FCSTD DOCUMENT  (FreeCAD 0.16R6712 (Git))
Label: connector panels
License: All rights reserved
LicenseURL: http://en.wikipedia.org/wiki/All_rights_reserved
objects: Sketcher::SketchObject×2
note: 2 computed .brp shape members not serialized (recipe doc carries the construction recipe); baked Part::Feature solids carry a one-line shape summary decoded from their .brp

FEATURE [Sketcher::SketchObject] Sketch  label="motors"
  sketch-geometry (109):
    g0: LineSegment StartX=-80 StartY=50 StartZ=0 EndX=80 EndY=50 EndZ=0
    g1: LineSegment StartX=85 StartY=45 StartZ=0 EndX=85 EndY=-45 EndZ=0
    g2: LineSegment StartX=80 StartY=-50 StartZ=0 EndX=-80 EndY=-50 EndZ=0
    g3: LineSegment StartX=-85 StartY=-45 StartZ=0 EndX=-85 EndY=45 EndZ=0
    g4: LineSegment [constr] StartX=-80 StartY=40 StartZ=0 EndX=80 EndY=40 EndZ=0
    g5: LineSegment [constr] StartX=80 StartY=40 StartZ=0 EndX=80 EndY=-40 EndZ=0
    g6: LineSegment [constr] StartX=80 StartY=-40 StartZ=0 EndX=-80 EndY=-40 EndZ=0
    g7: LineSegment [constr] StartX=-80 StartY=-40 StartZ=0 EndX=-80 EndY=40 EndZ=0
    g8: LineSegment [constr] StartX=-80 StartY=40 StartZ=0 EndX=-80 EndY=45 EndZ=0
    g9: LineSegment [constr] StartX=80 StartY=40 StartZ=0 EndX=80 EndY=45 EndZ=0
    g10: LineSegment [constr] StartX=80 StartY=-40 StartZ=0 EndX=80 EndY=-45 EndZ=0
    g11: LineSegment [constr] StartX=-80 StartY=-40 StartZ=0 EndX=-80 EndY=-45 EndZ=0
    g12: Circle CenterX=-80 CenterY=45 CenterZ=0 NormalX=0 NormalY=0 NormalZ=1 Radius=1.5
    g13: Circle CenterX=80 CenterY=45 CenterZ=0 NormalX=0 NormalY=0 NormalZ=1 Radius=1.5
    g14: Circle CenterX=80 CenterY=-45 CenterZ=0 NormalX=0 NormalY=0 NormalZ=1 Radius=1.5
    g15: Circle CenterX=-80 CenterY=-45 CenterZ=0 NormalX=0 NormalY=0 NormalZ=1 Radius=1.5
    g16: LineSegment StartX=-63.2009 StartY=-7.15277 StartZ=0 EndX=-59.4009 EndY=-7.82282 EndZ=0
    g17: LineSegment StartX=-57.1698 StartY=-10.4818 StartZ=0 EndX=-57.1698 EndY=-21.6417 EndZ=0
    g18: LineSegment StartX=-59.4009 StartY=-24.3007 StartZ=0 EndX=-63.2009 EndY=-24.9707 EndZ=0
    g19: LineSegment StartX=-66.3698 StartY=-22.3118 StartZ=0 EndX=-66.3698 EndY=-9.81175 EndZ=0
    g20: ArcOfCircle CenterX=-59.8698 CenterY=-10.4818 CenterZ=0 NormalX=0 NormalY=0 NormalZ=1 Radius=2.7 StartAngle=0 EndAngle=1.39626
    g21: ArcOfCircle CenterX=-63.6698 CenterY=-9.81175 CenterZ=0 NormalX=0 NormalY=0 NormalZ=1 Radius=2.7 StartAngle=1.39626 EndAngle=3.14159
    g22: ArcOfCircle CenterX=-59.8698 CenterY=-21.6417 CenterZ=0 NormalX=0 NormalY=0 NormalZ=1 Radius=2.7 StartAngle=4.88692 EndAngle=6.28319
    g23: ArcOfCircle CenterX=-63.6698 CenterY=-22.3118 CenterZ=0 NormalX=0 NormalY=0 NormalZ=1 Radius=2.7 StartAngle=3.14159 EndAngle=4.88692
    g24: Circle CenterX=-61.7698 CenterY=-3.6506 CenterZ=0 NormalX=0 NormalY=0 NormalZ=1 Radius=1.5
    g25: Circle CenterX=-61.7698 CenterY=-28.6506 CenterZ=0 NormalX=0 NormalY=0 NormalZ=1 Radius=1.5
    g26: LineSegment [constr] StartX=-61.7698 StartY=-3.6506 StartZ=0 EndX=-61.7698 EndY=-28.6506 EndZ=0
    g27: Circle CenterX=-61.7698 CenterY=21.3494 CenterZ=0 NormalX=0 NormalY=0 NormalZ=1 Radius=8
    g28: LineSegment [constr] StartX=-61.7698 StartY=21.3494 StartZ=0 EndX=-61.7698 EndY=-3.6506 EndZ=0
    g29: LineSegment [constr] StartX=80 StartY=-45 StartZ=0 EndX=-80 EndY=-45 EndZ=0
    g30: LineSegment [constr] StartX=-80 StartY=45 StartZ=0 EndX=80 EndY=45 EndZ=0
    g31: Circle CenterX=0 CenterY=45 CenterZ=0 NormalX=0 NormalY=0 NormalZ=1 Radius=1.5
    g32: Circle CenterX=0 CenterY=-45 CenterZ=0 NormalX=0 NormalY=0 NormalZ=1 Radius=1.5
    g33: Circle CenterX=-30.8849 CenterY=21.3494 CenterZ=0 NormalX=0 NormalY=0 NormalZ=1 Radius=8
    g34: LineSegment [constr] StartX=-30.8849 StartY=21.3494 StartZ=0 EndX=-30.8849 EndY=-3.6506 EndZ=0
    g35: Circle CenterX=0 CenterY=21.3494 CenterZ=0 NormalX=0 NormalY=0 NormalZ=1 Radius=8
    g36: LineSegment [constr] StartX=0 StartY=21.3494 StartZ=0 EndX=0 EndY=-3.6506 EndZ=0
    g37: Circle CenterX=30.8849 CenterY=21.3494 CenterZ=0 NormalX=0 NormalY=0 NormalZ=1 Radius=8
    g38: LineSegment [constr] StartX=30.8849 StartY=21.3494 StartZ=0 EndX=30.8849 EndY=-3.6506 EndZ=0
    g39: Circle CenterX=61.7698 CenterY=21.3494 CenterZ=0 NormalX=0 NormalY=0 NormalZ=1 Radius=10
    g40: LineSegment [constr] StartX=-80 StartY=21.3494 StartZ=0 EndX=-61.7698 EndY=21.3494 EndZ=0
    g41: LineSegment [constr] StartX=-61.7698 StartY=21.3494 StartZ=0 EndX=-30.8849 EndY=21.3494 EndZ=0
    g42: LineSegment [constr] StartX=-30.8849 StartY=21.3494 StartZ=0 EndX=0 EndY=21.3494 EndZ=0
    g43: LineSegment [constr] StartX=0 StartY=21.3494 StartZ=0 EndX=30.8849 EndY=21.3494 EndZ=0
    g44: LineSegment [constr] StartX=30.8849 StartY=21.3494 StartZ=0 EndX=61.7698 EndY=21.3494 EndZ=0
    g45: LineSegment [constr] StartX=61.7698 StartY=21.3494 StartZ=0 EndX=80 EndY=21.3494 EndZ=0
    g46: LineSegment [constr] StartX=61.7698 StartY=21.3494 StartZ=0 EndX=61.7698 EndY=-15.6506 EndZ=0
    g47: Circle CenterX=61.7698 CenterY=-15.6506 CenterZ=0 NormalX=0 NormalY=0 NormalZ=1 Radius=1.5
    g48: LineSegment [constr] StartX=-63.6698 StartY=-7.11175 StartZ=0 EndX=-61.7698 EndY=-7.11175 EndZ=0
    g49: LineSegment [constr] StartX=-63.6698 StartY=-25.0118 StartZ=0 EndX=-61.7698 EndY=-25.0118 EndZ=0
    g50: LineSegment [constr] StartX=-66.3698 StartY=-21.6417 StartZ=0 EndX=-61.7698 EndY=-21.6417 EndZ=0
    g51: LineSegment [constr] StartX=-61.7698 StartY=-21.6417 StartZ=0 EndX=-57.1698 EndY=-21.6417 EndZ=0
    g52: LineSegment [constr] StartX=-63.2009 StartY=-24.9707 StartZ=0 EndX=-61.7698 EndY=-28.6506 EndZ=0
    g53: LineSegment [constr] StartX=-63.6698 StartY=-7.11175 StartZ=0 EndX=-61.7698 EndY=-3.6506 EndZ=0
    g54: LineSegment StartX=-32.316 StartY=-7.15277 StartZ=0 EndX=-28.516 EndY=-7.82282 EndZ=0
    g55: LineSegment StartX=-26.2849 StartY=-10.4818 StartZ=0 EndX=-26.2849 EndY=-21.6417 EndZ=0
    g56: LineSegment StartX=-28.516 StartY=-24.3007 StartZ=0 EndX=-32.316 EndY=-24.9707 EndZ=0
    g57: LineSegment StartX=-35.4849 StartY=-22.3118 StartZ=0 EndX=-35.4849 EndY=-9.81175 EndZ=0
    g58: ArcOfCircle CenterX=-28.9849 CenterY=-10.4818 CenterZ=0 NormalX=0 NormalY=0 NormalZ=1 Radius=2.7 StartAngle=0 EndAngle=1.39626
    g59: ArcOfCircle CenterX=-32.7849 CenterY=-9.81175 CenterZ=0 NormalX=0 NormalY=0 NormalZ=1 Radius=2.7 StartAngle=1.39626 EndAngle=3.14159
    g60: ArcOfCircle CenterX=-28.9849 CenterY=-21.6417 CenterZ=0 NormalX=0 NormalY=0 NormalZ=1 Radius=2.7 StartAngle=4.88692 EndAngle=6.28319
    g61: ArcOfCircle CenterX=-32.7849 CenterY=-22.3118 CenterZ=0 NormalX=0 NormalY=0 NormalZ=1 Radius=2.7 StartAngle=3.14159 EndAngle=4.88692
    g62: Circle CenterX=-30.8849 CenterY=-3.6506 CenterZ=0 NormalX=0 NormalY=0 NormalZ=1 Radius=1.5
    g63: Circle CenterX=-30.8849 CenterY=-28.6506 CenterZ=0 NormalX=0 NormalY=0 NormalZ=1 Radius=1.5
    g64: LineSegment [constr] StartX=-30.8849 StartY=-3.6506 StartZ=0 EndX=-30.8849 EndY=-28.6506 EndZ=0
    g65: LineSegment [constr] StartX=-32.7849 StartY=-7.11175 StartZ=0 EndX=-30.8849 EndY=-7.11175 EndZ=0
    g66: LineSegment [constr] StartX=-32.7849 StartY=-25.0118 StartZ=0 EndX=-30.8849 EndY=-25.0118 EndZ=0
    g67: LineSegment [constr] StartX=-35.4849 StartY=-21.6417 StartZ=0 EndX=-30.8849 EndY=-21.6417 EndZ=0
    g68: LineSegment [constr] StartX=-30.8849 StartY=-21.6417 StartZ=0 EndX=-26.2849 EndY=-21.6417 EndZ=0
    g69: LineSegment [constr] StartX=-32.316 StartY=-24.9707 StartZ=0 EndX=-30.8849 EndY=-28.6506 EndZ=0
    g70: LineSegment [constr] StartX=-32.7849 StartY=-7.11175 StartZ=0 EndX=-30.8849 EndY=-3.6506 EndZ=0
    g71: LineSegment StartX=-1.43115 StartY=-7.15277 StartZ=0 EndX=2.36885 EndY=-7.82282 EndZ=0
    g72: LineSegment StartX=4.6 StartY=-10.4818 StartZ=0 EndX=4.6 EndY=-21.6417 EndZ=0
    g73: LineSegment StartX=2.36885 StartY=-24.3007 StartZ=0 EndX=-1.43115 EndY=-24.9707 EndZ=0
    g74: LineSegment StartX=-4.6 StartY=-22.3118 StartZ=0 EndX=-4.6 EndY=-9.81175 EndZ=0
    g75: ArcOfCircle CenterX=1.9 CenterY=-10.4818 CenterZ=0 NormalX=0 NormalY=0 NormalZ=1 Radius=2.7 StartAngle=0 EndAngle=1.39626
    g76: ArcOfCircle CenterX=-1.9 CenterY=-9.81175 CenterZ=0 NormalX=0 NormalY=0 NormalZ=1 Radius=2.7 StartAngle=1.39626 EndAngle=3.14159
    g77: ArcOfCircle CenterX=1.9 CenterY=-21.6417 CenterZ=0 NormalX=0 NormalY=0 NormalZ=1 Radius=2.7 StartAngle=4.88692 EndAngle=6.28319
    g78: ArcOfCircle CenterX=-1.9 CenterY=-22.3118 CenterZ=0 NormalX=0 NormalY=0 NormalZ=1 Radius=2.7 StartAngle=3.14159 EndAngle=4.88692
    g79: Circle CenterX=0 CenterY=-3.6506 CenterZ=0 NormalX=0 NormalY=0 NormalZ=1 Radius=1.5
    g80: Circle CenterX=0 CenterY=-28.6506 CenterZ=0 NormalX=0 NormalY=0 NormalZ=1 Radius=1.5
    g81: LineSegment [constr] StartX=0 StartY=-3.6506 StartZ=0 EndX=0 EndY=-28.6506 EndZ=0
    g82: LineSegment [constr] StartX=-1.9 StartY=-7.11175 StartZ=0 EndX=0 EndY=-7.11175 EndZ=0
    g83: LineSegment [constr] StartX=-1.9 StartY=-25.0118 StartZ=0 EndX=0 EndY=-25.0118 EndZ=0
    g84: LineSegment [constr] StartX=-4.6 StartY=-21.6417 StartZ=0 EndX=0 EndY=-21.6417 EndZ=0
    g85: LineSegment [constr] StartX=0 StartY=-21.6417 StartZ=0 EndX=4.6 EndY=-21.6417 EndZ=0
    g86: LineSegment [constr] StartX=-1.43115 StartY=-24.9707 StartZ=0 EndX=0 EndY=-28.6506 EndZ=0
    g87: LineSegment [constr] StartX=-1.9 StartY=-7.11175 StartZ=0 EndX=0 EndY=-3.6506 EndZ=0
    g88: LineSegment StartX=29.4538 StartY=-7.15277 StartZ=0 EndX=33.2538 EndY=-7.82282 EndZ=0
    g89: LineSegment StartX=35.4849 StartY=-10.4818 StartZ=0 EndX=35.4849 EndY=-21.6417 EndZ=0
    g90: LineSegment StartX=33.2538 StartY=-24.3007 StartZ=0 EndX=29.4538 EndY=-24.9707 EndZ=0
    g91: LineSegment StartX=26.2849 StartY=-22.3118 StartZ=0 EndX=26.2849 EndY=-9.81175 EndZ=0
    g92: ArcOfCircle CenterX=32.7849 CenterY=-10.4818 CenterZ=0 NormalX=0 NormalY=0 NormalZ=1 Radius=2.7 StartAngle=0 EndAngle=1.39626
    g93: ArcOfCircle CenterX=28.9849 CenterY=-9.81175 CenterZ=0 NormalX=0 NormalY=0 NormalZ=1 Radius=2.7 StartAngle=1.39626 EndAngle=3.14159
    g94: ArcOfCircle CenterX=32.7849 CenterY=-21.6417 CenterZ=0 NormalX=0 NormalY=0 NormalZ=1 Radius=2.7 StartAngle=4.88692 EndAngle=6.28319
    g95: ArcOfCircle CenterX=28.9849 CenterY=-22.3118 CenterZ=0 NormalX=0 NormalY=0 NormalZ=1 Radius=2.7 StartAngle=3.14159 EndAngle=4.88692
    g96: Circle CenterX=30.8849 CenterY=-3.6506 CenterZ=0 NormalX=0 NormalY=0 NormalZ=1 Radius=1.5
    g97: Circle CenterX=30.8849 CenterY=-28.6506 CenterZ=0 NormalX=0 NormalY=0 NormalZ=1 Radius=1.5
    g98: LineSegment [constr] StartX=30.8849 StartY=-3.6506 StartZ=0 EndX=30.8849 EndY=-28.6506 EndZ=0
    g99: LineSegment [constr] StartX=28.9849 StartY=-7.11175 StartZ=0 EndX=30.8849 EndY=-7.11175 EndZ=0
    g100: LineSegment [constr] StartX=28.9849 StartY=-25.0118 StartZ=0 EndX=30.8849 EndY=-25.0118 EndZ=0
    g101: LineSegment [constr] StartX=26.2849 StartY=-21.6417 StartZ=0 EndX=30.8849 EndY=-21.6417 EndZ=0
    g102: LineSegment [constr] StartX=30.8849 StartY=-21.6417 StartZ=0 EndX=35.4849 EndY=-21.6417 EndZ=0
    g103: LineSegment [constr] StartX=29.4538 StartY=-24.9707 StartZ=0 EndX=30.8849 EndY=-28.6506 EndZ=0
    g104: LineSegment [constr] StartX=28.9849 StartY=-7.11175 StartZ=0 EndX=30.8849 EndY=-3.6506 EndZ=0
    g105: ArcOfCircle CenterX=-80 CenterY=45 CenterZ=0 NormalX=0 NormalY=0 NormalZ=1 Radius=5 StartAngle=1.5708 EndAngle=3.14159
    g106: ArcOfCircle CenterX=80 CenterY=45 CenterZ=0 NormalX=0 NormalY=0 NormalZ=1 Radius=5 StartAngle=0 EndAngle=1.5708
    g107: ArcOfCircle CenterX=80 CenterY=-45 CenterZ=0 NormalX=0 NormalY=0 NormalZ=1 Radius=5 StartAngle=4.71239 EndAngle=6.28319
    g108: ArcOfCircle CenterX=-80 CenterY=-45 CenterZ=0 NormalX=0 NormalY=0 NormalZ=1 Radius=5 StartAngle=3.14159 EndAngle=4.71239
  constraints (292):
    c: Horizontal(g0)
    c: Horizontal(g2)
    c: Vertical(g1)
    c: Vertical(g3)
    c: Coincident(g4,g5)
    c: Coincident(g5,g6)
    c: Coincident(g6,g7)
    c: Coincident(g7,g4)
    c: Horizontal(g4)
    c: Horizontal(g6)
    c: Vertical(g7)
    c: Symmetric(g4,g5,g-1)
    c: Symmetric(g4,g4,g-2)
    c: DistanceY(g5,g5) = 80
    c: DistanceX(g4,g4) = 160
    c: Coincident(g8,g4)
    c: Vertical(g8)
    c: Coincident(g9,g4)
    c: Vertical(g9)
    c: Coincident(g10,g5)
    c: Vertical(g10)
    c: Coincident(g11,g6)
    c: Vertical(g11)
    c: Coincident(g12,g8)
    c: Coincident(g13,g9)
    c: Coincident(g14,g10)
    c: Coincident(g15,g11)
    c: Radius(g12) = 1.5
    c: Vertical(g17)
    c: Vertical(g19)
    c: Equal(g16,g18)
    c: Tangent(g17,g20) = 1.5708
    c: Tangent(g16,g20) = 1.5708
    c: Tangent(g16,g21) = 1.5708
    c: Tangent(g19,g21) = 1.5708
    c: Tangent(g17,g22) = 1.5708
    c: Tangent(g18,g22) = 1.5708
    c: Tangent(g18,g23) = 1.5708
    c: Tangent(g19,g23) = 1.5708
    c: Equal(g21,g23)
    c: Equal(g22,g20)
    c: Coincident(g26,g24)
    c: Coincident(g26,g25)
    c: Vertical(g26)
    c: DistanceY(g26,g26) = 25
    c: Radius(g20) = 2.7
    c: Equal(g21,g20)
    c: Coincident(g28,g27)
    c: Coincident(g28,g24)
    c: Vertical(g28)
    c: DistanceY(g28,g28) = 25
    c: Radius(g27) = 8
    c: Symmetric(g8,g11,g-1)
    c: Symmetric(g9,g10,g-1)
    c: Coincident(g29,g10)
    c: Coincident(g29,g11)
    c: Horizontal(g29)
    c: Coincident(g30,g8)
    c: Coincident(g30,g9)
    c: PointOnObject(g31,g30)
    c: PointOnObject(g31,g-2)
    c: PointOnObject(g32,g29)
    c: PointOnObject(g32,g-2)
    c: Equal(g12,g31)
    c: Equal(g12,g13)
    c: Equal(g12,g14)
    c: Equal(g12,g32)
    c: Equal(g12,g15)
    c: Radius(g24) = 1.5
    c: Equal(g24,g25)
    c: Coincident(g34,g33)
    c: Vertical(g34)
    c: Equal(g28,g34) = 25
    c: Equal(g27,g33) = 8
    c: Coincident(g36,g35)
    c: Vertical(g36)
    c: Equal(g28,g36) = 25
    c: Equal(g27,g35) = 8
    c: Coincident(g38,g37)
    c: Vertical(g38)
    c: Equal(g28,g38) = 25
    c: Equal(g27,g37) = 8
    c: Radius(g39) = 10
    c: PointOnObject(g40,g7)
    c: Coincident(g40,g27)
    c: Horizontal(g40)
    c: Coincident(g41,g27)
    c: Coincident(g41,g33)
    c: Horizontal(g41)
    c: Coincident(g42,g33)
    c: Coincident(g42,g35)
    c: Horizontal(g42)
    c: Coincident(g43,g35)
    c: Coincident(g43,g37)
    c: Horizontal(g43)
    c: Coincident(g44,g37)
    c: Coincident(g44,g39)
    c: Horizontal(g44)
    c: Coincident(g45,g39)
    c: PointOnObject(g45,g5)
    c: Horizontal(g45)
    c: Equal(g41,g42)
    c: Equal(g42,g43)
    c: Equal(g43,g44)
    c: Equal(g45,g40)
    c: Coincident(g46,g39)
    c: Vertical(g46)
    c: Coincident(g47,g46)
    c: DistanceY(g46,g46) = 37
    c: DistanceX(g42,g42) = 30.8849
    c: DistanceX(g40,g40) = 18.2302
    c: DistanceY(g45,g4) = 18.6506
    c: Radius(g47) = 1.5
    c: PointOnObject(g48,g21)
    c: PointOnObject(g48,g26)
    c: Horizontal(g48)
    c: Tangent(g48,g21)
    c: PointOnObject(g49,g23)
    c: PointOnObject(g49,g26)
    c: Horizontal(g49)
    c: Tangent(g49,g23)
    c: DistanceY(g49,g48) = 17.9
    c: DistanceX(g19,g17) = 9.2
    c: PointOnObject(g50,g19)
    c: PointOnObject(g50,g26)
    c: Horizontal(g50)
    c: Coincident(g51,g50)
    c: PointOnObject(g51,g17)
    c: Horizontal(g51)
    c: Equal(g51,g50)
    c: Coincident(g52,g18)
    c: Coincident(g52,g25)
    c: Coincident(g53,g48)
    c: Coincident(g53,g24)
    c: Equal(g53,g52)
    c: Coincident(g51,g17)
    c: Equal(g49,g48)
    c: Angle(g16,g48) = 0.174533
    c: Vertical(g55)
    c: Vertical(g57)
    c: Equal(g54,g56)
    c: Tangent(g55,g58) = 1.5708
    c: Tangent(g54,g58) = 1.5708
    c: Tangent(g54,g59) = 1.5708
    c: Tangent(g57,g59) = 1.5708
    c: Tangent(g55,g60) = 1.5708
    c: Tangent(g56,g60) = 1.5708
    c: Tangent(g56,g61) = 1.5708
    c: Tangent(g57,g61) = 1.5708
    c: Equal(g59,g61)
    c: Equal(g60,g58)
    c: Coincident(g64,g62)
    c: Coincident(g64,g63)
    c: Vertical(g64)
    c: Equal(g26,g64) = 25
    c: Equal(g20,g58) = 2.7
    c: Equal(g59,g58)
    c: Equal(g24,g62) = 1.5
    c: Equal(g62,g63)
    c: PointOnObject(g65,g64)
    c: Horizontal(g65)
    c: Tangent(g65,g59)
    c: PointOnObject(g66,g61)
    c: PointOnObject(g66,g64)
    c: Horizontal(g66)
    c: Tangent(g66,g61)
    c: DistanceY(g66,g65) = 17.9
    c: DistanceX(g57,g55) = 9.2
    c: PointOnObject(g67,g57)
    c: PointOnObject(g67,g64)
    c: Horizontal(g67)
    c: Coincident(g68,g67)
    c: PointOnObject(g68,g55)
    c: Horizontal(g68)
    c: Equal(g68,g67)
    c: Coincident(g69,g56)
    c: Coincident(g69,g63)
    c: Coincident(g70,g65)
    c: Coincident(g70,g62)
    c: Equal(g70,g69)
    c: Coincident(g68,g55)
    c: Equal(g66,g65)
    c: Angle(g54,g65) = 0.174533
    c: Coincident(g62,g34)
    c: Vertical(g72)
    c: Vertical(g74)
    c: Equal(g71,g73)
    c: Tangent(g72,g75) = 1.5708
    c: Tangent(g71,g75) = 1.5708
    c: Tangent(g71,g76) = 1.5708
    c: Tangent(g74,g76) = 1.5708
    c: Tangent(g72,g77) = 1.5708
    c: Tangent(g73,g77) = 1.5708
    c: Tangent(g73,g78) = 1.5708
    c: Tangent(g74,g78) = 1.5708
    c: Equal(g76,g78)
    c: Equal(g77,g75)
    c: Coincident(g81,g79)
    c: Coincident(g81,g80)
    c: Vertical(g81)
    c: Equal(g26,g81) = 25
    c: Equal(g20,g75) = 2.7
    c: Equal(g76,g75)
    c: Equal(g24,g79) = 1.5
    c: Equal(g79,g80)
    c: PointOnObject(g82,g81)
    c: Horizontal(g82)
    c: Tangent(g82,g76)
    c: PointOnObject(g83,g78)
    c: PointOnObject(g83,g81)
    c: Horizontal(g83)
    c: Tangent(g83,g78)
    c: DistanceY(g83,g82) = 17.9
    c: DistanceX(g74,g72) = 9.2
    c: PointOnObject(g84,g74)
    c: PointOnObject(g84,g81)
    c: Horizontal(g84)
    c: Coincident(g85,g84)
    c: PointOnObject(g85,g72)
    c: Horizontal(g85)
    c: Equal(g85,g84)
    c: Coincident(g86,g73)
    c: Coincident(g86,g80)
    c: Coincident(g87,g82)
    c: Coincident(g87,g79)
    c: Equal(g87,g86)
    c: Coincident(g85,g72)
    c: Equal(g83,g82)
    c: Angle(g71,g82) = 0.174533
    c: Coincident(g79,g36)
    c: Vertical(g89)
    c: Vertical(g91)
    c: Equal(g88,g90)
    c: Tangent(g89,g92) = 1.5708
    c: Tangent(g88,g92) = 1.5708
    c: Tangent(g88,g93) = 1.5708
    c: Tangent(g91,g93) = 1.5708
    c: Tangent(g89,g94) = 1.5708
    c: Tangent(g90,g94) = 1.5708
    c: Tangent(g90,g95) = 1.5708
    c: Tangent(g91,g95) = 1.5708
    c: Equal(g93,g95)
    c: Equal(g94,g92)
    c: Coincident(g98,g96)
    c: Coincident(g98,g97)
    c: Vertical(g98)
    c: Equal(g26,g98) = 25
    c: Equal(g20,g92) = 2.7
    c: Equal(g93,g92)
    c: Equal(g24,g96) = 1.5
    c: Equal(g96,g97)
    c: PointOnObject(g99,g98)
    c: Horizontal(g99)
    c: Tangent(g99,g93)
    c: PointOnObject(g100,g95)
    c: PointOnObject(g100,g98)
    c: Horizontal(g100)
    c: Tangent(g100,g95)
    c: DistanceY(g100,g99) = 17.9
    c: DistanceX(g91,g89) = 9.2
    c: PointOnObject(g101,g91)
    c: PointOnObject(g101,g98)
    c: Horizontal(g101)
    c: Coincident(g102,g101)
    c: PointOnObject(g102,g89)
    c: Horizontal(g102)
    c: Equal(g102,g101)
    c: Coincident(g103,g90)
    c: Coincident(g103,g97)
    c: Coincident(g104,g99)
    c: Coincident(g104,g96)
    c: Equal(g104,g103)
    c: Coincident(g102,g89)
    c: Equal(g100,g99)
    c: Angle(g88,g99) = 0.174533
    c: Coincident(g96,g38)
    c: Tangent(g3,g105) = 1.5708
    c: Tangent(g0,g105) = 1.5708
    c: Tangent(g0,g106) = 1.5708
    c: Tangent(g1,g106) = 1.5708
    c: Tangent(g1,g107) = 1.5708
    c: Tangent(g2,g107) = 1.5708
    c: Tangent(g2,g108) = 1.5708
    c: Tangent(g3,g108) = 1.5708
    c: DistanceX(g3,g1) = 170
    c: DistanceY(g2,g0) = 100
    c: Radius(g105) = 5
    c: Equal(g105,g106)
    c: Equal(g105,g107)
    c: Equal(g105,g108)
    c: Coincident(g107,g10)
    c: Coincident(g105,g8)
FEATURE [Sketcher::SketchObject] Sketch001  label="controls"
  sketch-geometry (51):
    g0: LineSegment StartX=-85 StartY=40 StartZ=0 EndX=85 EndY=40 EndZ=0
    g1: LineSegment StartX=90 StartY=35 StartZ=0 EndX=90 EndY=-35 EndZ=0
    g2: LineSegment StartX=85 StartY=-40 StartZ=0 EndX=-85 EndY=-40 EndZ=0
    g3: LineSegment StartX=-90 StartY=-35 StartZ=0 EndX=-90 EndY=35 EndZ=0
    g4: LineSegment [constr] StartX=-80 StartY=30 StartZ=0 EndX=80 EndY=30 EndZ=0
    g5: LineSegment [constr] StartX=80 StartY=30 StartZ=0 EndX=80 EndY=-30 EndZ=0
    g6: LineSegment [constr] StartX=80 StartY=-30 StartZ=0 EndX=-80 EndY=-30 EndZ=0
    g7: LineSegment [constr] StartX=-80 StartY=-30 StartZ=0 EndX=-80 EndY=30 EndZ=0
    g8: LineSegment [constr] StartX=-80 StartY=30 StartZ=0 EndX=-85 EndY=35 EndZ=0
    g9: LineSegment [constr] StartX=80 StartY=30 StartZ=0 EndX=85 EndY=35 EndZ=0
    g10: LineSegment [constr] StartX=80 StartY=-30 StartZ=0 EndX=85 EndY=-35 EndZ=0
    g11: LineSegment [constr] StartX=-80 StartY=-30 StartZ=0 EndX=-85 EndY=-35 EndZ=0
    g12: Circle CenterX=-85 CenterY=35 CenterZ=0 NormalX=0 NormalY=0 NormalZ=1 Radius=1.5
    g13: Circle CenterX=85 CenterY=35 CenterZ=0 NormalX=0 NormalY=0 NormalZ=1 Radius=1.5
    g14: Circle CenterX=85 CenterY=-35 CenterZ=0 NormalX=0 NormalY=0 NormalZ=1 Radius=1.5
    g15: Circle CenterX=-85 CenterY=-35 CenterZ=0 NormalX=0 NormalY=0 NormalZ=1 Radius=1.5
    g16: LineSegment StartX=-29.8863 StartY=12.1283 StartZ=0 EndX=-26.0863 EndY=11.4583 EndZ=0
    g17: LineSegment StartX=-23.8552 StartY=8.79931 StartZ=0 EndX=-23.8552 EndY=-10.9606 EndZ=0
    g18: LineSegment StartX=-26.0863 StartY=-13.6196 StartZ=0 EndX=-29.8863 EndY=-14.2896 EndZ=0
    g19: LineSegment StartX=-33.0552 StartY=-11.6307 StartZ=0 EndX=-33.0552 EndY=9.46935 EndZ=0
    g20: ArcOfCircle CenterX=-26.5552 CenterY=8.79931 CenterZ=0 NormalX=0 NormalY=0 NormalZ=1 Radius=2.7 StartAngle=0 EndAngle=1.39626
    g21: ArcOfCircle CenterX=-30.3552 CenterY=9.46935 CenterZ=0 NormalX=0 NormalY=0 NormalZ=1 Radius=2.7 StartAngle=1.39626 EndAngle=3.14159
    g22: ArcOfCircle CenterX=-26.5552 CenterY=-10.9606 CenterZ=0 NormalX=0 NormalY=0 NormalZ=1 Radius=2.7 StartAngle=4.88692 EndAngle=6.28319
    g23: ArcOfCircle CenterX=-30.3552 CenterY=-11.6307 CenterZ=0 NormalX=0 NormalY=0 NormalZ=1 Radius=2.7 StartAngle=3.14159 EndAngle=4.88692
    g24: Circle CenterX=-28.4552 CenterY=15.4757 CenterZ=0 NormalX=0 NormalY=0 NormalZ=1 Radius=1.5
    g25: Circle CenterX=-28.4552 CenterY=-17.8243 CenterZ=0 NormalX=0 NormalY=0 NormalZ=1 Radius=1.5
    g26: LineSegment [constr] StartX=-28.4552 StartY=15.4757 StartZ=0 EndX=-28.4552 EndY=-17.8243 EndZ=0
    g27: LineSegment [constr] StartX=85 StartY=-35 StartZ=0 EndX=-85 EndY=-35 EndZ=0
    g28: LineSegment [constr] StartX=-85 StartY=35 StartZ=0 EndX=85 EndY=35 EndZ=0
    g29: Circle CenterX=0 CenterY=35 CenterZ=0 NormalX=0 NormalY=0 NormalZ=1 Radius=1.5
    g30: Circle CenterX=0 CenterY=-35 CenterZ=0 NormalX=0 NormalY=0 NormalZ=1 Radius=1.5
    g31: LineSegment [constr] StartX=-30.3552 StartY=12.1693 StartZ=0 EndX=-28.4552 EndY=12.1693 EndZ=0
    g32: LineSegment [constr] StartX=-30.3552 StartY=-14.3307 StartZ=0 EndX=-28.4552 EndY=-14.3307 EndZ=0
    g33: LineSegment [constr] StartX=-33.0552 StartY=-10.9606 StartZ=0 EndX=-28.4552 EndY=-10.9606 EndZ=0
    g34: LineSegment [constr] StartX=-28.4552 StartY=-10.9606 StartZ=0 EndX=-23.8552 EndY=-10.9606 EndZ=0
    g35: LineSegment [constr] StartX=-29.8863 StartY=-14.2896 StartZ=0 EndX=-28.4552 EndY=-17.8243 EndZ=0
    g36: LineSegment [constr] StartX=-30.3552 StartY=12.1693 StartZ=0 EndX=-28.4552 EndY=15.4757 EndZ=0
    g37: ArcOfCircle CenterX=-85 CenterY=35 CenterZ=0 NormalX=0 NormalY=0 NormalZ=1 Radius=5 StartAngle=1.5708 EndAngle=3.14159
    g38: ArcOfCircle CenterX=85 CenterY=35 CenterZ=0 NormalX=0 NormalY=0 NormalZ=1 Radius=5 StartAngle=0 EndAngle=1.5708
    g39: ArcOfCircle CenterX=85 CenterY=-35 CenterZ=0 NormalX=0 NormalY=0 NormalZ=1 Radius=5 StartAngle=4.71239 EndAngle=6.28319
    g40: ArcOfCircle CenterX=-85 CenterY=-35 CenterZ=0 NormalX=0 NormalY=0 NormalZ=1 Radius=5 StartAngle=3.14159 EndAngle=4.71239
    g41: Circle CenterX=-61.845 CenterY=12.405 CenterZ=0 NormalX=0 NormalY=0 NormalZ=1 Radius=1.75055
    g42: Circle CenterX=-61.845 CenterY=-15.2998 CenterZ=0 NormalX=0 NormalY=0 NormalZ=1 Radius=1.43894
    g43: LineSegment StartX=-68.539 StartY=6.21778 StartZ=0 EndX=-55.151 EndY=6.21778 EndZ=0
    g44: LineSegment StartX=-55.151 StartY=6.21778 StartZ=0 EndX=-55.151 EndY=-9.11262 EndZ=0
    g45: LineSegment StartX=-55.151 StartY=-9.11262 StartZ=0 EndX=-68.539 EndY=-9.11262 EndZ=0
    g46: LineSegment StartX=-68.539 StartY=-9.11262 StartZ=0 EndX=-68.539 EndY=6.21778 EndZ=0
    g47: LineSegment [constr] StartX=-68.539 StartY=6.21778 StartZ=0 EndX=-61.845 EndY=12.405 EndZ=0
    g48: LineSegment [constr] StartX=-61.845 StartY=12.405 StartZ=0 EndX=-55.151 EndY=6.21778 EndZ=0
    g49: LineSegment [constr] StartX=-68.539 StartY=-9.11262 StartZ=0 EndX=-61.845 EndY=-15.2998 EndZ=0
    g50: LineSegment [constr] StartX=-61.845 StartY=-15.2998 StartZ=0 EndX=-55.151 EndY=-9.11262 EndZ=0
  constraints (125):
    c: Horizontal(g0)
    c: Horizontal(g2)
    c: Vertical(g1)
    c: Vertical(g3)
    c: Coincident(g4,g5)
    c: Coincident(g5,g6)
    c: Coincident(g6,g7)
    c: Coincident(g7,g4)
    c: Horizontal(g4)
    c: Horizontal(g6)
    c: Vertical(g7)
    c: Symmetric(g4,g5,g-1)
    c: Symmetric(g4,g4,g-2)
    c: DistanceY(g5,g5) = 60
    c: DistanceX(g4,g4) = 160
    c: Coincident(g8,g4)
    c: Coincident(g9,g4)
    c: Coincident(g10,g5)
    c: Coincident(g11,g6)
    c: Coincident(g12,g8)
    c: Coincident(g13,g9)
    c: Coincident(g14,g10)
    c: Coincident(g15,g11)
    c: Radius(g12) = 1.5
    c: Vertical(g17)
    c: Vertical(g19)
    c: Equal(g16,g18)
    c: Tangent(g17,g20) = 1.5708
    c: Tangent(g16,g20) = 1.5708
    c: Tangent(g16,g21) = 1.5708
    c: Tangent(g19,g21) = 1.5708
    c: Tangent(g17,g22) = 1.5708
    c: Tangent(g18,g22) = 1.5708
    c: Tangent(g18,g23) = 1.5708
    c: Tangent(g19,g23) = 1.5708
    c: Equal(g21,g23)
    c: Equal(g22,g20)
    c: Coincident(g26,g24)
    c: Coincident(g26,g25)
    c: Vertical(g26)
    c: DistanceY(g26,g26) = 33.3
    c: Radius(g20) = 2.7
    c: Equal(g21,g20)
    c: Symmetric(g8,g11,g-1)
    c: Symmetric(g9,g10,g-1)
    c: Coincident(g27,g10)
    c: Coincident(g27,g11)
    c: Horizontal(g27)
    c: Coincident(g28,g8)
    c: Coincident(g28,g9)
    c: PointOnObject(g29,g28)
    c: PointOnObject(g29,g-2)
    c: PointOnObject(g30,g27)
    c: PointOnObject(g30,g-2)
    c: Equal(g12,g29)
    c: Equal(g12,g13)
    c: Equal(g12,g14)
    c: Equal(g12,g30)
    c: Equal(g12,g15)
    c: Radius(g24) = 1.5
    c: Equal(g24,g25)
    c: PointOnObject(g31,g21)
    c: PointOnObject(g31,g26)
    c: Horizontal(g31)
    c: Tangent(g31,g21)
    c: PointOnObject(g32,g23)
    c: PointOnObject(g32,g26)
    c: Horizontal(g32)
    c: Tangent(g32,g23)
    c: DistanceY(g32,g31) = 26.5
    c: DistanceX(g19,g17) = 9.2
    c: PointOnObject(g33,g19)
    c: PointOnObject(g33,g26)
    c: Horizontal(g33)
    c: Coincident(g34,g33)
    c: PointOnObject(g34,g17)
    c: Horizontal(g34)
    c: Equal(g34,g33)
    c: Coincident(g35,g18)
    c: Coincident(g35,g25)
    c: Coincident(g36,g31)
    c: Coincident(g36,g24)
    c: Equal(g36,g35)
    c: Coincident(g34,g17)
    c: Equal(g32,g31)
    c: Angle(g16,g31) = 0.174533
    c: Tangent(g3,g37) = 1.5708
    c: Tangent(g0,g37) = 1.5708
    c: Tangent(g0,g38) = 1.5708
    c: Tangent(g1,g38) = 1.5708
    c: Tangent(g1,g39) = 1.5708
    c: Tangent(g2,g39) = 1.5708
    c: Tangent(g2,g40) = 1.5708
    c: Tangent(g3,g40) = 1.5708
    c: DistanceX(g3,g1) = 180
    c: DistanceY(g2,g0) = 80
    c: Radius(g37) = 5
    c: Equal(g37,g38)
    c: Equal(g37,g39)
    c: Equal(g37,g40)
    c: Coincident(g39,g10)
    c: Coincident(g37,g8)
    c: Coincident(g43,g44)
    c: Coincident(g44,g45)
    c: Coincident(g45,g46)
    c: Coincident(g46,g43)
    c: Horizontal(g43)
    c: Horizontal(g45)
    c: Vertical(g44)
    c: Vertical(g46)
    c: Coincident(g47,g43)
    c: Coincident(g47,g41)
    c: Coincident(g48,g41)
    c: Coincident(g48,g43)
    c: Coincident(g49,g45)
    c: Coincident(g49,g42)
    c: Coincident(g50,g42)
    c: Coincident(g50,g44)
    c: Equal(g50,g49)
    c: Equal(g49,g47)
    c: Equal(g47,g48)
    c: Angle(g11,g6) = 2.35619
    c: DistanceY(g42,g41) = 27.7048
    c: DistanceY(g46,g46) = 15.3304
    c: DistanceX(g45,g45) = 13.388
